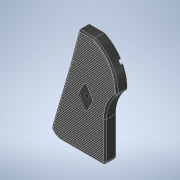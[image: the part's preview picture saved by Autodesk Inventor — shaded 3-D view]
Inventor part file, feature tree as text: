
AUTODESK INVENTOR PART (.ipt)
format: ipt  version: 2021 (Build 250183000, 183)  size: 552,960 bytes
history: native  units: in
note: dims shown in document units (in); Inventor stores cm internally (conversion verified against a paired STEP export)
features: extrude x9, sketch x9, fillet x4, projected_geometry x2, thread x1
ambient origin geometry x8: Origin, YZ Plane, XZ Plane, XY Plane, X Axis, Y Axis, Z Axis, Center Point
bodies: Solid1 (feature_tree)
feature tree (25):
  extrude  "Extrusion1"  Depth=2.7165in
  extrude  "Extrusion2"  Depth=0.2756in TaperAngle=0.0deg
  extrude  "Extrusion7"  Depth=0.1969in
  fillet  "Fillet11"  Radius=0.1969in
  fillet  "Fillet12"  Radius=0.3543in
  fillet  "Fillet14"  Radius=0.3543in
  extrude  "Extrusion10"  Depth=0.0394in
  fillet  "Fillet15"  Radius=0.0787in
  extrude  "Extrusion15"  Depth=0.1181in
  thread  "Thread3"  [1 undecoded]
  extrude  "Extrusão16"  Depth=0.0394in
  extrude  "Extrusão17"  Depth=0.0394in
  extrude  "Extrusão18"  Depth=0.0394in
  extrude  "Extrusão19"  Depth=0.0394in
  sketch  "Sketch1"  dims[d0=1.7717in d1=2.7165in]
  sketch  "Sketch2"  dims[d7=0.2756in d8=0.0in d14=0.0591in d15=0.0in]
  sketch  "Sketch8"  dims[d19=0.1181in]
  sketch  "Sketch12"  dims[d101=7.874in d103=0.3937in d105=7.874in d107=0.3937in d109=7.874in d111=0.3937in d113=7.874in d115=0.3937in d117=7.874in d119=0.3937in d121=7.874in d123=0.3937in d125=7.874in d127=0.3937in d129=7.874in d131=0.3937in d173=0.1969in d174=0.1969in d175=0.3543in d176=0.3543in]
  projected_geometry  "Projected Loop5"
  sketch  "Sketch13"  dims[d177=0.0315in d178=0.0in d185=0.0394in d186=0.0787in]
  projected_geometry  "Projected Loop8"
  sketch  "Esboço17"  dims[d191=0.0787in d195=0.1181in d196=0.0787in]
  sketch  "Esboço18"  dims[d197=0.1565in d198=0.0in d199=0.0394in]
  sketch  "Esboço19"  dims[d903=0.0394in d904=0.0394in]
  sketch  "Esboço20"  dims[d905=0.0394in d906=0.0394in d907=0.0394in d908=0.0394in d909=0.0394in d910=0.0394in d911=0.0394in d912=0.0394in d913=0.0394in d914=0.0394in d915=0.0394in d916=0.0394in d932=0.0394in d933=0.0394in d934=0.0394in d935=0.0394in d936=0.0394in d937=0.0394in d938=0.0394in d939=0.0394in d940=0.0394in d941=0.0394in d942=0.0394in d943=0.0394in d944=0.0394in d945=0.0394in d946=0.0394in d948=0.0394in d954=0.0394in d958=0.0394in d959=0.0394in d960=0.0039in d961=0.0in d962=0.3937in d963=0.0in d966=0.1575in d967=0.0in d970=0.0594in d971=0.0in d972=0.0594in d973=0.0in d974=2.0523in d975=0.1969in d976=0.0in]
note: 1 required parameter value undecoded (feature->parameter linkage not recoverable at this tier; creation-order binding heuristic only, values carry confidence <= 0.55)
